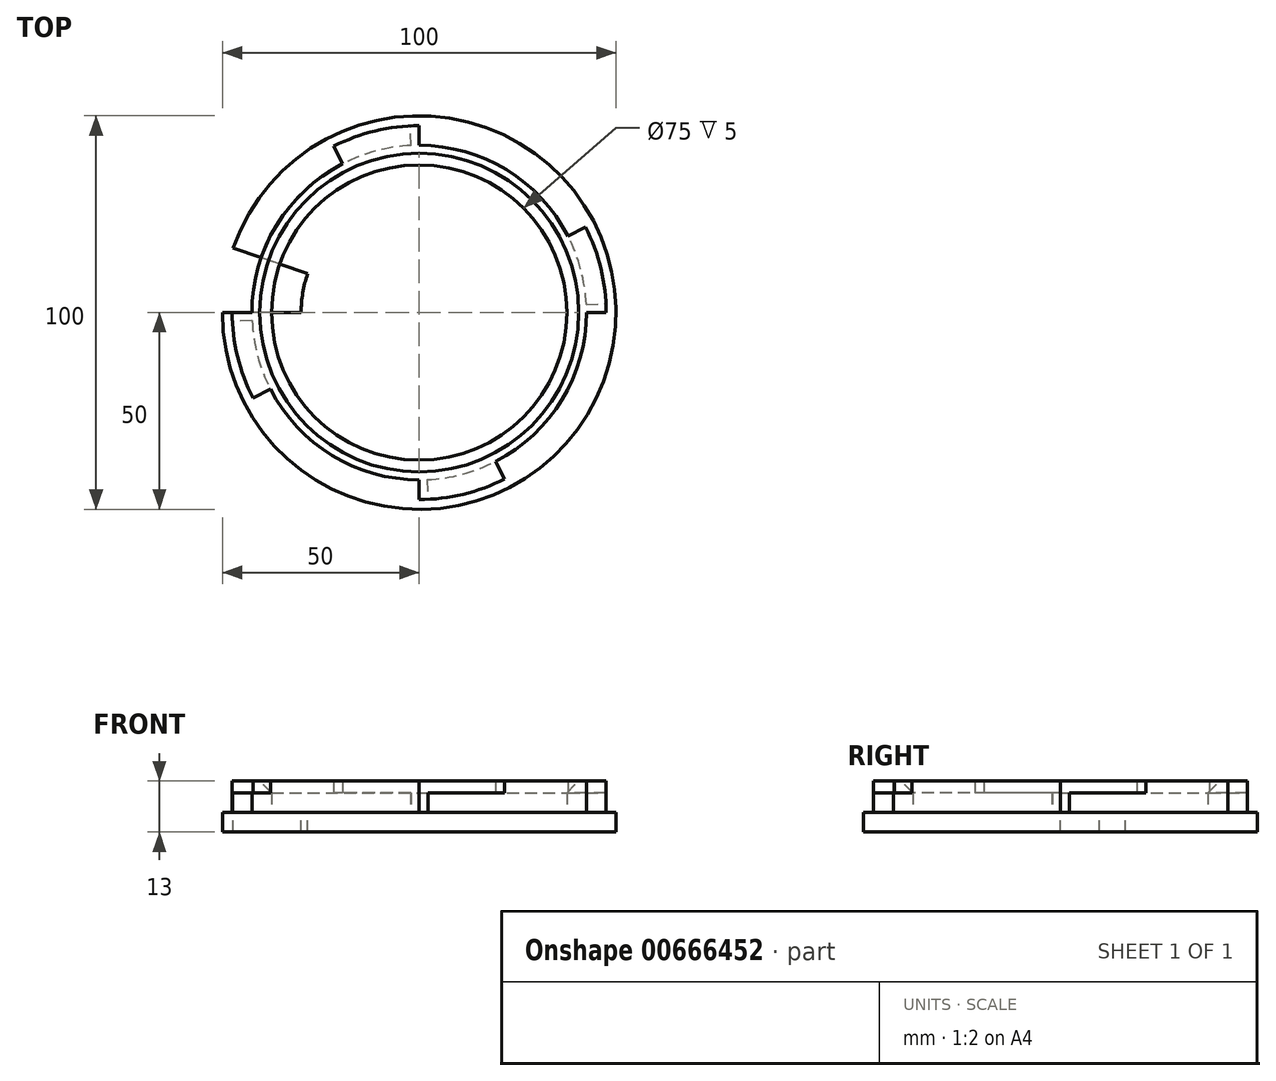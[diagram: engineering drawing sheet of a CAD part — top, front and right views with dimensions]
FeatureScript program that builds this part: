
annotation { "Feature Type Name" : "Feature", "Feature Type Description" : "" }
export const myFeature = defineFeature(function(context is Context, id is Id, definition is map)
    precondition{}
    {
        {
            var Q0;
            Q0=qCreatedBy(makeId("Top.planeOp"),FACE);
            var sketch = newSketch(context, id + "F0", { "sketchPlane" : qUnion([Q0])});
            skCircle(sketch, "E0", {"center": v(0, 0) * mm, "radius": 50 * mm});
            skCircle(sketch, "E1", {"center": v(0, 0) * mm, "radius": 47.5 * mm});
            skLineSegment(sketch, "E2", {"start": v(0, 42.5) * mm, "end": v(0, 47.5) * mm});
            skArc(sketch, "E3", {"start": v(0, 42.5) * mm, "mid": v(-10, 41.3) * mm, "end": v(-19.44, 37.8) * mm});
            skLineSegment(sketch, "E4", {"start": v(-19.44, 37.8) * mm, "end": v(-21.73, 42.24) * mm});
            skLineSegment(sketch, "E5", {"start": v(-2, 42.45) * mm, "end": v(-2.24, 47.45) * mm});
            skLineSegment(sketch, "E6.1.0", {"start": v(-37.8, -19.44) * mm, "end": v(-42.24, -21.73) * mm});
            skArc(sketch, "E6.1.1", {"start": v(-42.5, 0) * mm, "mid": v(-41.3, -10) * mm, "end": v(-37.8, -19.44) * mm});
            skLineSegment(sketch, "E6.1.2", {"start": v(-42.5, 0) * mm, "end": v(-47.5, 0) * mm});
            skLineSegment(sketch, "E6.1.3", {"start": v(-42.45, -2) * mm, "end": v(-47.45, -2.24) * mm});
            skLineSegment(sketch, "E6.2.0", {"start": v(19.44, -37.8) * mm, "end": v(21.73, -42.24) * mm});
            skArc(sketch, "E6.2.1", {"start": v(0, -42.5) * mm, "mid": v(10, -41.3) * mm, "end": v(19.44, -37.8) * mm});
            skLineSegment(sketch, "E6.2.2", {"start": v(0, -42.5) * mm, "end": v(0, -47.5) * mm});
            skLineSegment(sketch, "E6.2.3", {"start": v(2, -42.45) * mm, "end": v(2.24, -47.45) * mm});
            skLineSegment(sketch, "E6.3.0", {"start": v(37.8, 19.44) * mm, "end": v(42.24, 21.73) * mm});
            skArc(sketch, "E6.3.1", {"start": v(42.5, 0) * mm, "mid": v(41.3, 10) * mm, "end": v(37.8, 19.44) * mm});
            skLineSegment(sketch, "E6.3.2", {"start": v(42.5, 0) * mm, "end": v(47.5, 0) * mm});
            skLineSegment(sketch, "E6.3.3", {"start": v(42.45, 2) * mm, "end": v(47.45, 2.24) * mm});
            skCircle(sketch, "E7", {"center": v(0, 0) * mm, "radius": 42.5 * mm});
            skLineSegment(sketch, "E8", {"start": v(-37.8, -19.44) * mm, "end": v(-33.35, -17.15) * mm});
            skCircle(sketch, "E9", {"center": v(0, 0) * mm, "radius": 37.5 * mm});
            skSolve(sketch);
        }
        {
            var Q0;
            Q0=makeQuery(id+"F0.imprint","IMPRINT",FACE,{"disambiguationData":[TD([[makeQuery(id+"F0.imprint","IMPRINT",EDGE,{"derivedFrom":sQuery(id+"F0.wireOp",EDGE,"E9")}),-1.0]])]});
            extrude(context, id + "F1", {"entities" : qUnion([Q0]), "depth" : 8 * mm, "offsetDistance" : 25 * mm});
        }
        {
            var Q0;
            {var subQ0=sQuery(id+"F0.wireOp",EDGE,"E6.1.2");Q0=makeQuery(id+"F0.imprint","IMPRINT",FACE,{"disambiguationData":[TD([[makeQuery(id+"F0.imprint","IMPRINT",EDGE,{"derivedFrom":subQ0}),1.0]])]});}
            var Q1;
            {var subQ0=sQuery(id+"F0.wireOp",EDGE,"E2");Q1=makeQuery(id+"F0.imprint","IMPRINT",FACE,{"disambiguationData":[TD([[makeQuery(id+"F0.imprint","IMPRINT",EDGE,{"derivedFrom":subQ0}),1.0]])]});}
            var Q2;
            {var subQ0=sQuery(id+"F0.wireOp",EDGE,"E6.3.2");Q2=makeQuery(id+"F0.imprint","IMPRINT",FACE,{"disambiguationData":[TD([[makeQuery(id+"F0.imprint","IMPRINT",EDGE,{"derivedFrom":subQ0}),1.0]])]});}
            var Q3;
            {var subQ0=sQuery(id+"F0.wireOp",EDGE,"E6.2.2");Q3=makeQuery(id+"F0.imprint","IMPRINT",FACE,{"disambiguationData":[TD([[makeQuery(id+"F0.imprint","IMPRINT",EDGE,{"derivedFrom":subQ0}),1.0]])]});}
            extrude(context, id + "F2", {"entities" : qUnion([Q0, Q1, Q2, Q3]), "operationType" : NewBodyOperationType.ADD, "depth" : 8 * mm, "offsetDistance" : 25 * mm});
        }
        {
            var Q0;
            {var subQ0=sQuery(id+"F0.wireOp",EDGE,"E6.1.0");Q0=makeQuery(id+"F0.imprint","IMPRINT",FACE,{"disambiguationData":[TD([[makeQuery(id+"F0.imprint","IMPRINT",EDGE,{"derivedFrom":subQ0}),-1.0]])]});}
            var Q1;
            {var subQ0=sQuery(id+"F0.wireOp",EDGE,"E6.2.0");Q1=makeQuery(id+"F0.imprint","IMPRINT",FACE,{"disambiguationData":[TD([[makeQuery(id+"F0.imprint","IMPRINT",EDGE,{"derivedFrom":subQ0}),-1.0]])]});}
            var Q2;
            {var subQ0=sQuery(id+"F0.wireOp",EDGE,"E6.3.0");Q2=makeQuery(id+"F0.imprint","IMPRINT",FACE,{"disambiguationData":[TD([[makeQuery(id+"F0.imprint","IMPRINT",EDGE,{"derivedFrom":subQ0}),-1.0]])]});}
            var Q3;
            {var subQ0=sQuery(id+"F0.wireOp",EDGE,"E4");Q3=makeQuery(id+"F0.imprint","IMPRINT",FACE,{"disambiguationData":[TD([[makeQuery(id+"F0.imprint","IMPRINT",EDGE,{"derivedFrom":subQ0}),-1.0]])]});}
            extrude(context, id + "F3", {"entities" : qUnion([Q0, Q1, Q2, Q3]), "operationType" : NewBodyOperationType.ADD, "depth" : 8 * mm, "offsetDistance" : 25 * mm, "hasSecondDirection" : true, "secondDirectionOppositeDirection" : true, "secondDirectionDepth" : -5 * mm});
        }
        {
            var Q0;
            Q0=qCreatedBy(makeId("Top.planeOp"),FACE);
            var sketch = newSketch(context, id + "F4", { "sketchPlane" : qUnion([Q0])});
            skCircle(sketch, "E10", {"center": v(0, 0) * mm, "radius": 50 * mm});
            skSolve(sketch);
        }
        {
            var Q0;
            Q0 = qSketchRegion(id + "F4", true);
            extrude(context, id + "F5", {"entities" : qUnion([Q0]), "operationType" : NewBodyOperationType.ADD, "depth" : -5 * mm, "offsetDistance" : 25 * mm});
        }
        {
            var Q0;
            Q0=qCreatedBy(makeId("Top.planeOp"),FACE);
            var sketch = newSketch(context, id + "F6", { "sketchPlane" : qUnion([Q0])});
            skArc(sketch, "E11", {"start": v(-47.22, 16.43) * mm, "mid": v(-49.3, 8.33) * mm, "end": v(-50, 0) * mm});
            skArc(sketch, "E12", {"start": v(-30, 0) * mm, "mid": v(-29.58, 5) * mm, "end": v(-28.33, 9.86) * mm});
            skLineSegment(sketch, "E13", {"start": v(-28.33, 9.86) * mm, "end": v(-47.22, 16.43) * mm});
            skLineSegment(sketch, "E14", {"start": v(-30, 0) * mm, "end": v(-50, 0) * mm});
            skSolve(sketch);
        }
        {
            var Q0;
            Q0 = qSketchRegion(id + "F6", true);
            extrude(context, id + "F7", {"entities" : qUnion([Q0]), "operationType" : NewBodyOperationType.REMOVE, "oppositeDirection" : true, "depth" : 5 * mm, "offsetDistance" : 25 * mm});
        }
        {
            var Q0;
            Q0=makeQuery(id+"F1.opExtrude","CAP_EDGE",EDGE,{"disambiguationData":[OSD([sQuery(id+"F0.wireOp",EDGE,"E9")])],"isStart":false});
            chamfer(context, id + "F8", {"entities" : qUnion([Q0]), "width" : 3 * mm, "tangentPropagation" : true});
        }
    });
